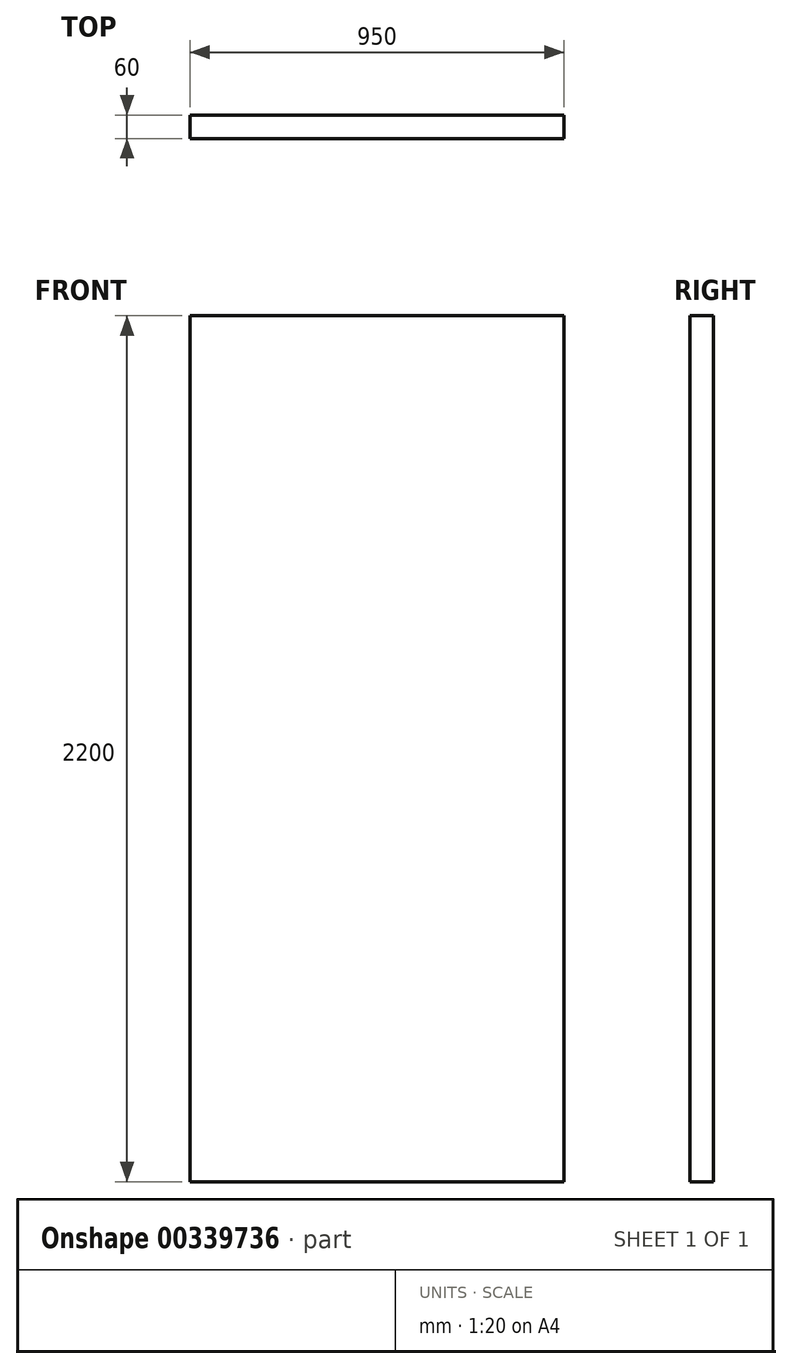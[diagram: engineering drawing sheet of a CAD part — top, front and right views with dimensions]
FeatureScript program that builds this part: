
annotation { "Feature Type Name" : "Feature", "Feature Type Description" : "" }
export const myFeature = defineFeature(function(context is Context, id is Id, definition is map)
    precondition{}
    {
        {
            var Q0;
            Q0=qCreatedBy(makeId("Top.planeOp"),FACE);
            var sketch = newSketch(context, id + "F0", { "sketchPlane" : qUnion([Q0])});
            skLineSegment(sketch, "E0.bottom", {"start": v(-38.56, 30) * mm, "end": v(911.44, 30) * mm});
            skLineSegment(sketch, "E0.top", {"start": v(-38.56, -30) * mm, "end": v(911.44, -30) * mm});
            skLineSegment(sketch, "E0.left", {"start": v(-38.56, 30) * mm, "end": v(-38.56, -30) * mm});
            skLineSegment(sketch, "E0.right", {"start": v(911.44, 30) * mm, "end": v(911.44, -30) * mm});
            skSolve(sketch);
        }
        {
            var Q0;
            Q0 = qSketchRegion(id + "F0", true);
            extrude(context, id + "F1", {"entities" : qUnion([Q0]), "depth" : 2200 * mm});
        }
    });
